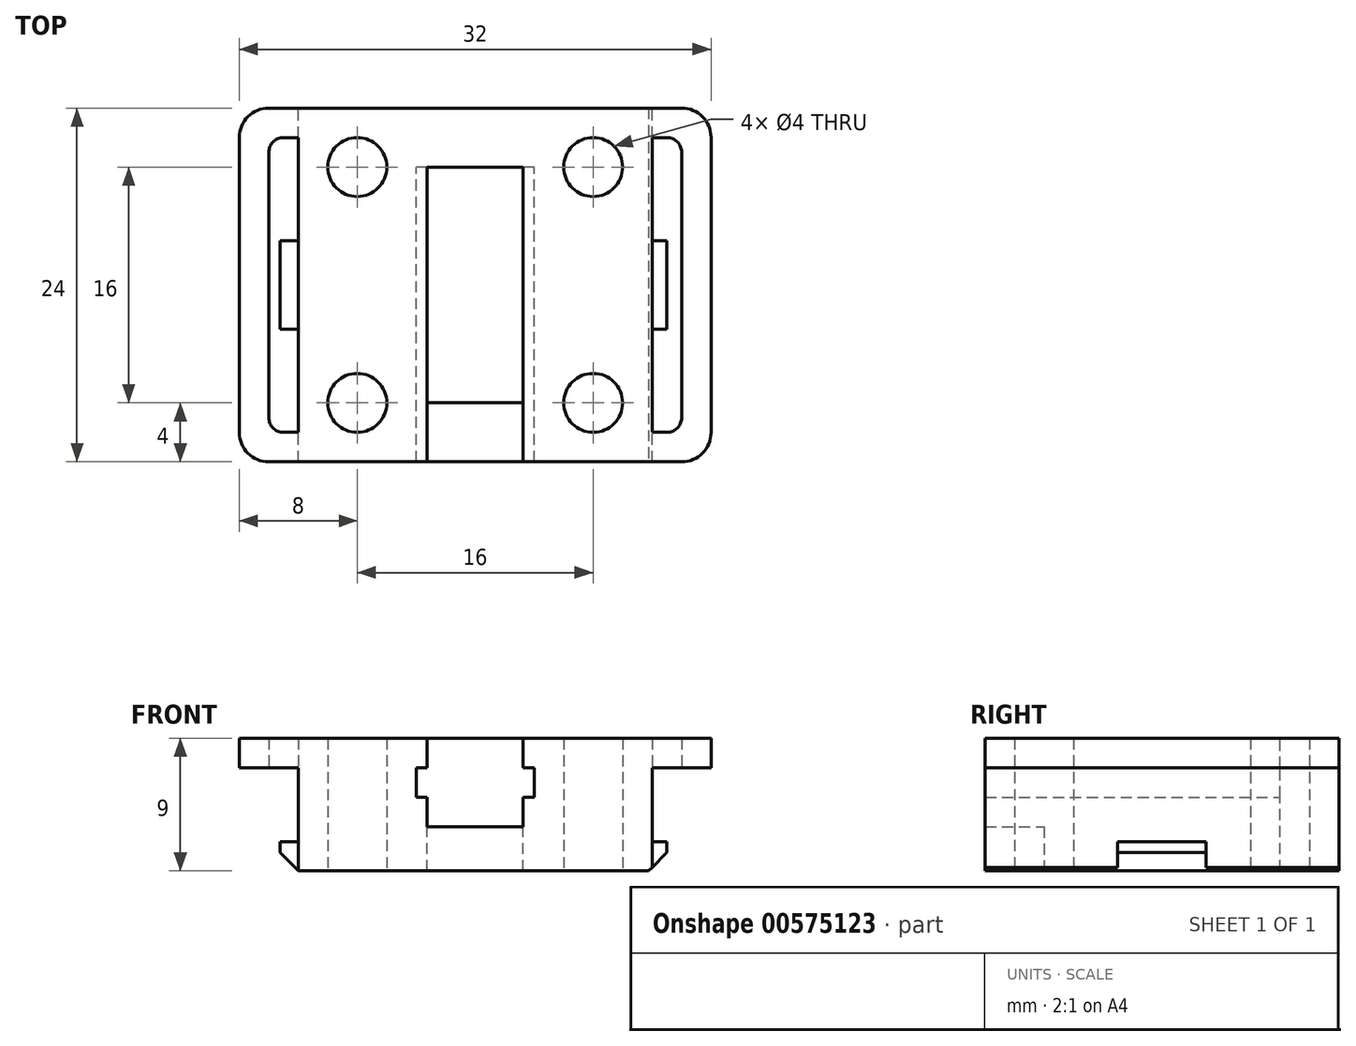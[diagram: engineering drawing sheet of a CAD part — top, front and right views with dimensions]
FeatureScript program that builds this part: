
annotation { "Feature Type Name" : "Feature", "Feature Type Description" : "" }
export const myFeature = defineFeature(function(context is Context, id is Id, definition is map)
    precondition{}
    {
        {
            var Q0;
            Q0=qCreatedBy(makeId("Top.planeOp"),FACE);
            var sketch = newSketch(context, id + "F0", { "sketchPlane" : qUnion([Q0])});
            skLineSegment(sketch, "E0.bottom", {"start": v(12, -12) * mm, "end": v(-12, -12) * mm});
            skLineSegment(sketch, "E0.top", {"start": v(12, 12) * mm, "end": v(-12, 12) * mm});
            skLineSegment(sketch, "E0.left", {"start": v(12, -12) * mm, "end": v(12, 12) * mm});
            skLineSegment(sketch, "E0.right", {"start": v(-12, -12) * mm, "end": v(-12, 12) * mm});
            skPoint(sketch, "E0.middle", {"position": v(0, 0) * mm});
            skCircle(sketch, "E1", {"center": v(-8, -8) * mm, "radius": 2 * mm});
            skCircle(sketch, "E2.0.1.0", {"center": v(-8, 8) * mm, "radius": 2 * mm});
            skCircle(sketch, "E2.1.0.0", {"center": v(8, -8) * mm, "radius": 2 * mm});
            skCircle(sketch, "E2.1.1.0", {"center": v(8, 8) * mm, "radius": 2 * mm});
            skLineSegment(sketch, "E2.direction1", {"start": v(-8, -8) * mm, "end": v(8, -8) * mm, "construction": true});
            skLineSegment(sketch, "E2.direction2", {"start": v(-8, -8) * mm, "end": v(-8, 8) * mm, "construction": true});
            skSolve(sketch);
        }
        {
            var Q0;
            Q0 = qSketchRegion(id + "F0", true);
            extrude(context, id + "F1", {"entities" : qUnion([Q0]), "depth" : 9 * mm, "offsetDistance" : 25 * mm});
        }
        {
            var Q0;
            Q0=qCreatedBy(makeId("Top.planeOp"),FACE);
            var sketch = newSketch(context, id + "F2", { "sketchPlane" : qUnion([Q0])});
            skLineSegment(sketch, "E3.bottom", {"start": v(16, -12) * mm, "end": v(-16, -12) * mm});
            skLineSegment(sketch, "E3.top", {"start": v(16, 12) * mm, "end": v(-16, 12) * mm});
            skLineSegment(sketch, "E3.left", {"start": v(16, -12) * mm, "end": v(16, 12) * mm});
            skLineSegment(sketch, "E3.right", {"start": v(-16, -12) * mm, "end": v(-16, 12) * mm});
            skPoint(sketch, "E3.middle", {"position": v(0, 0) * mm});
            skCircle(sketch, "E4", {"center": v(-8, -8) * mm, "radius": 2 * mm});
            skCircle(sketch, "E5.MirrorC", {"center": v(8, -8) * mm, "radius": 2 * mm});
            skCircle(sketch, "E6.MirrorC", {"center": v(-8, 8) * mm, "radius": 2 * mm});
            skCircle(sketch, "E7.MirrorC", {"center": v(8, 8) * mm, "radius": 2 * mm});
            skLineSegment(sketch, "E8.bottom", {"start": v(12, 10) * mm, "end": v(14, 10) * mm});
            skLineSegment(sketch, "E8.top", {"start": v(12, -10) * mm, "end": v(14, -10) * mm});
            skLineSegment(sketch, "E8.left", {"start": v(12, 10) * mm, "end": v(12, -10) * mm});
            skLineSegment(sketch, "E8.right", {"start": v(14, 10) * mm, "end": v(14, -10) * mm});
            skLineSegment(sketch, "E9.MirrorCS", {"start": v(-12, -10) * mm, "end": v(-14, -10) * mm});
            skLineSegment(sketch, "E10.MirrorCS", {"start": v(-14, 10) * mm, "end": v(-14, -10) * mm});
            skLineSegment(sketch, "E11.MirrorCS", {"start": v(-12, 10) * mm, "end": v(-14, 10) * mm});
            skLineSegment(sketch, "E12.MirrorCS", {"start": v(-12, 10) * mm, "end": v(-12, -10) * mm});
            skSolve(sketch);
        }
        {
            var Q0;
            Q0 = qSketchRegion(id + "F2", true);
            extrude(context, id + "F3", {"entities" : qUnion([Q0]), "operationType" : NewBodyOperationType.ADD, "depth" : 9 * mm, "offsetDistance" : 25 * mm, "hasSecondDirection" : true, "secondDirectionOppositeDirection" : false, "secondDirectionDepth" : 7 * mm});
        }
        {
            var Q0;
            Q0=qCreatedBy(makeId("Front.planeOp"),FACE);
            var sketch = newSketch(context, id + "F4", { "sketchPlane" : qUnion([Q0])});
            skLineSegment(sketch, "E13.bottom", {"start": v(4, 3) * mm, "end": v(-4, 3) * mm});
            skLineSegment(sketch, "E13.top", {"start": v(4, 9) * mm, "end": v(-4, 9) * mm});
            skLineSegment(sketch, "E13.left", {"start": v(4, 3) * mm, "end": v(4, 9) * mm});
            skLineSegment(sketch, "E13.right", {"start": v(-4, 3) * mm, "end": v(-4, 9) * mm});
            skPoint(sketch, "E13.middle", {"position": v(0, 6) * mm});
            skSolve(sketch);
        }
        {
            var Q0;
            Q0 = qSketchRegion(id + "F4", true);
            extrude(context, id + "F5", {"entities" : qUnion([Q0]), "operationType" : NewBodyOperationType.REMOVE, "depth" : 12 * mm, "offsetDistance" : 25 * mm});
        }
        {
            var Q0;
            Q0 = qSketchRegion(id + "F4", true);
            extrude(context, id + "F6", {"entities" : qUnion([Q0]), "operationType" : NewBodyOperationType.REMOVE, "oppositeDirection" : true, "depth" : 8 * mm, "offsetDistance" : 25 * mm});
        }
        {
            var Q0;
            Q0=qCreatedBy(makeId("Front.planeOp"),FACE);
            var sketch = newSketch(context, id + "F7", { "sketchPlane" : qUnion([Q0])});
            skLineSegment(sketch, "E14.bottom", {"start": v(-4, 9) * mm, "end": v(-3.25, 9) * mm});
            skLineSegment(sketch, "E14.top", {"start": v(-4, 7) * mm, "end": v(-3.25, 7) * mm});
            skLineSegment(sketch, "E14.left", {"start": v(-4, 9) * mm, "end": v(-4, 7) * mm});
            skLineSegment(sketch, "E14.right", {"start": v(-3.25, 9) * mm, "end": v(-3.25, 7) * mm});
            skLineSegment(sketch, "E15.bottom", {"start": v(3.25, 9) * mm, "end": v(4, 9) * mm});
            skLineSegment(sketch, "E15.top", {"start": v(3.25, 7) * mm, "end": v(4, 7) * mm});
            skLineSegment(sketch, "E15.left", {"start": v(3.25, 9) * mm, "end": v(3.25, 7) * mm});
            skLineSegment(sketch, "E15.right", {"start": v(4, 9) * mm, "end": v(4, 7) * mm});
            skLineSegment(sketch, "E16.bottom", {"start": v(3.25, 5) * mm, "end": v(4, 5) * mm});
            skLineSegment(sketch, "E16.top", {"start": v(3.25, 3) * mm, "end": v(4, 3) * mm});
            skLineSegment(sketch, "E16.left", {"start": v(3.25, 5) * mm, "end": v(3.25, 3) * mm});
            skLineSegment(sketch, "E16.right", {"start": v(4, 5) * mm, "end": v(4, 3) * mm});
            skLineSegment(sketch, "E17.bottom", {"start": v(-4, 5) * mm, "end": v(-3.25, 5) * mm});
            skLineSegment(sketch, "E17.top", {"start": v(-4, 3) * mm, "end": v(-3.25, 3) * mm});
            skLineSegment(sketch, "E17.left", {"start": v(-4, 5) * mm, "end": v(-4, 3) * mm});
            skLineSegment(sketch, "E17.right", {"start": v(-3.25, 5) * mm, "end": v(-3.25, 3) * mm});
            skSolve(sketch);
        }
        {
            var Q0;
            Q0 = qSketchRegion(id + "F7", true);
            extrude(context, id + "F8", {"entities" : qUnion([Q0]), "operationType" : NewBodyOperationType.ADD, "endBound" : BoundingType.SYMMETRIC, "depth" : 24 * mm, "offsetDistance" : 25 * mm});
        }
        {
            var Q0;
            Q0=qCreatedBy(makeId("Top.planeOp"),FACE);
            var sketch = newSketch(context, id + "F9", { "sketchPlane" : qUnion([Q0])});
            skLineSegment(sketch, "E18.bottom", {"start": v(-12, -3) * mm, "end": v(-13.25, -3) * mm});
            skLineSegment(sketch, "E18.top", {"start": v(-12, 3) * mm, "end": v(-13.25, 3) * mm});
            skLineSegment(sketch, "E18.left", {"start": v(-12, -3) * mm, "end": v(-12, 3) * mm});
            skLineSegment(sketch, "E18.right", {"start": v(-13.25, -3) * mm, "end": v(-13.25, 3) * mm});
            skPoint(sketch, "E18.middle", {"position": v(-12.62, 0) * mm});
            skLineSegment(sketch, "E19.1.0.0", {"start": v(11.75, -3) * mm, "end": v(11.75, 3) * mm});
            skLineSegment(sketch, "E19.1.0.1", {"start": v(13, -3) * mm, "end": v(13, 3) * mm});
            skPoint(sketch, "E19.1.0.2", {"position": v(12.38, 0) * mm});
            skLineSegment(sketch, "E19.1.0.3", {"start": v(13, 3) * mm, "end": v(11.75, 3) * mm});
            skLineSegment(sketch, "E19.1.0.4", {"start": v(13, -3) * mm, "end": v(11.75, -3) * mm});
            skLineSegment(sketch, "E19.direction1", {"start": v(-13.25, -3) * mm, "end": v(11.75, -3) * mm, "construction": true});
            skSolve(sketch);
        }
        {
            var Q0;
            Q0 = qSketchRegion(id + "F9", true);
            extrude(context, id + "F10", {"entities" : qUnion([Q0]), "operationType" : NewBodyOperationType.ADD, "depth" : 2 * mm, "offsetDistance" : 25 * mm});
        }
        {
            var Q0;
            Q0=makeQuery(id+"F10.opExtrude","CAP_EDGE",EDGE,{"disambiguationData":[OSD([sQuery(id+"F9.wireOp",EDGE,"E19.1.0.1")])],"isStart":true});
            var Q1;
            Q1=makeQuery(id+"F10.opExtrude","CAP_EDGE",EDGE,{"disambiguationData":[OSD([sQuery(id+"F9.wireOp",EDGE,"E18.right")])],"isStart":true});
            chamfer(context, id + "F11", {"entities" : qUnion([Q0, Q1]), "width" : 1.25 * mm, "tangentPropagation" : true});
        }
        {
            var Q0;
            Q0=qCreatedBy(makeId("Top.planeOp"),FACE);
            var sketch = newSketch(context, id + "F12", { "sketchPlane" : qUnion([Q0])});
            skLineSegment(sketch, "E20.bottom", {"start": v(3.25, -8) * mm, "end": v(-3.25, -8) * mm});
            skLineSegment(sketch, "E20.top", {"start": v(3.25, 8) * mm, "end": v(-3.25, 8) * mm});
            skLineSegment(sketch, "E20.left", {"start": v(3.25, -8) * mm, "end": v(3.25, 8) * mm});
            skLineSegment(sketch, "E20.right", {"start": v(-3.25, -8) * mm, "end": v(-3.25, 8) * mm});
            skPoint(sketch, "E20.middle", {"position": v(0, 0) * mm});
            skSolve(sketch);
        }
        {
            var Q0;
            Q0 = qSketchRegion(id + "F12", true);
            extrude(context, id + "F13", {"entities" : qUnion([Q0]), "operationType" : NewBodyOperationType.REMOVE, "depth" : 3 * mm, "offsetDistance" : 25 * mm});
        }
        {
            var Q0;
            Q0=makeQuery(id+"F3.opExtrude","SWEPT_EDGE",EDGE,{"disambiguationData":[OSD([sQuery(id+"F2.wireOp",EDGE,"E3.bottom"),sQuery(id+"F2.wireOp",EDGE,"E3.left")])]});
            var Q1;
            Q1=makeQuery(id+"F3.opExtrude","SWEPT_EDGE",EDGE,{"disambiguationData":[OSD([sQuery(id+"F2.wireOp",EDGE,"E3.top"),sQuery(id+"F2.wireOp",EDGE,"E3.left")])]});
            var Q2;
            Q2=makeQuery(id+"F3.opExtrude","SWEPT_EDGE",EDGE,{"disambiguationData":[OSD([sQuery(id+"F2.wireOp",EDGE,"E3.bottom"),sQuery(id+"F2.wireOp",EDGE,"E3.right")])]});
            var Q3;
            Q3=makeQuery(id+"F3.opExtrude","SWEPT_EDGE",EDGE,{"disambiguationData":[OSD([sQuery(id+"F2.wireOp",EDGE,"E3.top"),sQuery(id+"F2.wireOp",EDGE,"E3.right")])]});
            fillet(context, id + "F14", {"entities" : qUnion([Q0, Q1, Q2, Q3]), "radius" : 2 * mm, "tangentPropagation" : true, "allowEdgeOverflow" : false});
        }
        {
            var Q0;
            Q0=makeQuery(id+"F3.opExtrude","SWEPT_EDGE",EDGE,{"disambiguationData":[OSD([sQuery(id+"F2.wireOp",EDGE,"E10.MirrorCS"),sQuery(id+"F2.wireOp",EDGE,"E11.MirrorCS")])]});
            var Q1;
            Q1=makeQuery(id+"F3.opExtrude","SWEPT_EDGE",EDGE,{"disambiguationData":[OSD([sQuery(id+"F2.wireOp",EDGE,"E9.MirrorCS"),sQuery(id+"F2.wireOp",EDGE,"E10.MirrorCS")])]});
            var Q2;
            Q2=makeQuery(id+"F3.opExtrude","SWEPT_EDGE",EDGE,{"disambiguationData":[OSD([sQuery(id+"F2.wireOp",EDGE,"E8.bottom"),sQuery(id+"F2.wireOp",EDGE,"E8.right")])]});
            var Q3;
            Q3=makeQuery(id+"F3.opExtrude","SWEPT_EDGE",EDGE,{"disambiguationData":[OSD([sQuery(id+"F2.wireOp",EDGE,"E8.top"),sQuery(id+"F2.wireOp",EDGE,"E8.right")])]});
            fillet(context, id + "F15", {"entities" : qUnion([Q0, Q1, Q2, Q3]), "radius" : 1 * mm, "tangentPropagation" : true, "allowEdgeOverflow" : false});
        }
    });
